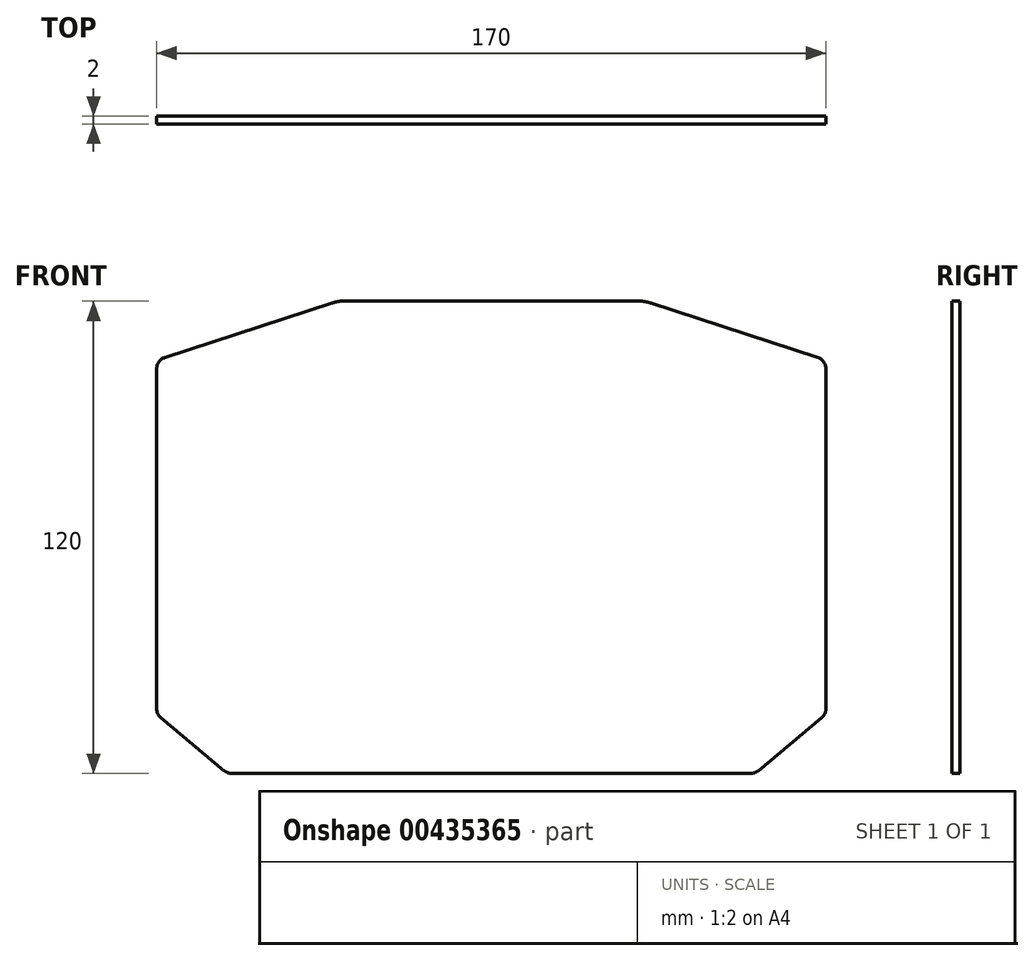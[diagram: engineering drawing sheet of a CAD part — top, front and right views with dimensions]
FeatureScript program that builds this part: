
annotation { "Feature Type Name" : "Feature", "Feature Type Description" : "" }
export const myFeature = defineFeature(function(context is Context, id is Id, definition is map)
    precondition{}
    {
        {
            var Q0;
            Q0=qCreatedBy(makeId("Front.planeOp"),FACE);
            var sketch = newSketch(context, id + "F0", { "sketchPlane" : qUnion([Q0])});
            skLineSegment(sketch, "E0", {"start": v(70.3, -49.77) * mm, "end": v(70.3, 36.65) * mm});
            skLineSegment(sketch, "E1", {"start": v(68.23, 39.5) * mm, "end": v(25.81, 53.34) * mm});
            skLineSegment(sketch, "E2", {"start": v(69.22, -52.07) * mm, "end": v(53.13, -65.48) * mm});
            skLineSegment(sketch, "E3", {"start": v(70.3, 38.83) * mm, "end": v(70.3, -31.17) * mm});
            skLineSegment(sketch, "E4", {"start": v(56.8, 43.23) * mm, "end": v(37.8, 49.43) * mm});
            skLineSegment(sketch, "E5.MirrorCS", {"start": v(-97.63, 39.5) * mm, "end": v(-55.21, 53.34) * mm});
            skLineSegment(sketch, "E6.MirrorCS", {"start": v(-98.62, -52.07) * mm, "end": v(-82.53, -65.48) * mm});
            skLineSegment(sketch, "E7.MirrorCS", {"start": v(-99.7, -49.77) * mm, "end": v(-99.7, 36.65) * mm});
            skLineSegment(sketch, "E8", {"start": v(-52.11, 53.83) * mm, "end": v(22.71, 53.83) * mm});
            skLineSegment(sketch, "E9", {"start": v(-80.61, -66.17) * mm, "end": v(51.21, -66.17) * mm});
            skArc(sketch, "E10", {"start": v(-99.7, 36.65) * mm, "mid": v(-99.13, 38.41) * mm, "end": v(-97.63, 39.5) * mm});
            skArc(sketch, "E11", {"start": v(-55.21, 53.34) * mm, "mid": v(-53.68, 53.7) * mm, "end": v(-52.11, 53.83) * mm});
            skArc(sketch, "E12", {"start": v(22.71, 53.83) * mm, "mid": v(24.28, 53.7) * mm, "end": v(25.81, 53.34) * mm});
            skArc(sketch, "E13", {"start": v(70.3, -49.77) * mm, "mid": v(70.02, -51.04) * mm, "end": v(69.22, -52.07) * mm});
            skArc(sketch, "E14", {"start": v(53.13, -65.48) * mm, "mid": v(52.24, -66) * mm, "end": v(51.21, -66.17) * mm});
            skArc(sketch, "E15", {"start": v(-80.61, -66.17) * mm, "mid": v(-81.64, -66) * mm, "end": v(-82.53, -65.48) * mm});
            skArc(sketch, "E16", {"start": v(-98.62, -52.07) * mm, "mid": v(-99.42, -51.04) * mm, "end": v(-99.7, -49.77) * mm});
            skArc(sketch, "E17", {"start": v(70.3, 36.65) * mm, "mid": v(69.73, 38.41) * mm, "end": v(68.23, 39.5) * mm});
            skSolve(sketch);
        }
        {
            var Q0;
            {var subQ2=sQuery(id+"F0.wireOp",EDGE,"E0");Q0=makeQuery(id+"F0.imprint","IMPRINT",FACE,{"disambiguationData":[TD([[makeQuery(id+"F0.imprint","IMPRINT",EDGE,{"derivedFrom":subQ2}),1.0]])]});}
            extrude(context, id + "F1", {"entities" : qUnion([Q0]), "depth" : 2 * mm, "offsetDistance" : 25 * mm});
        }
    });
